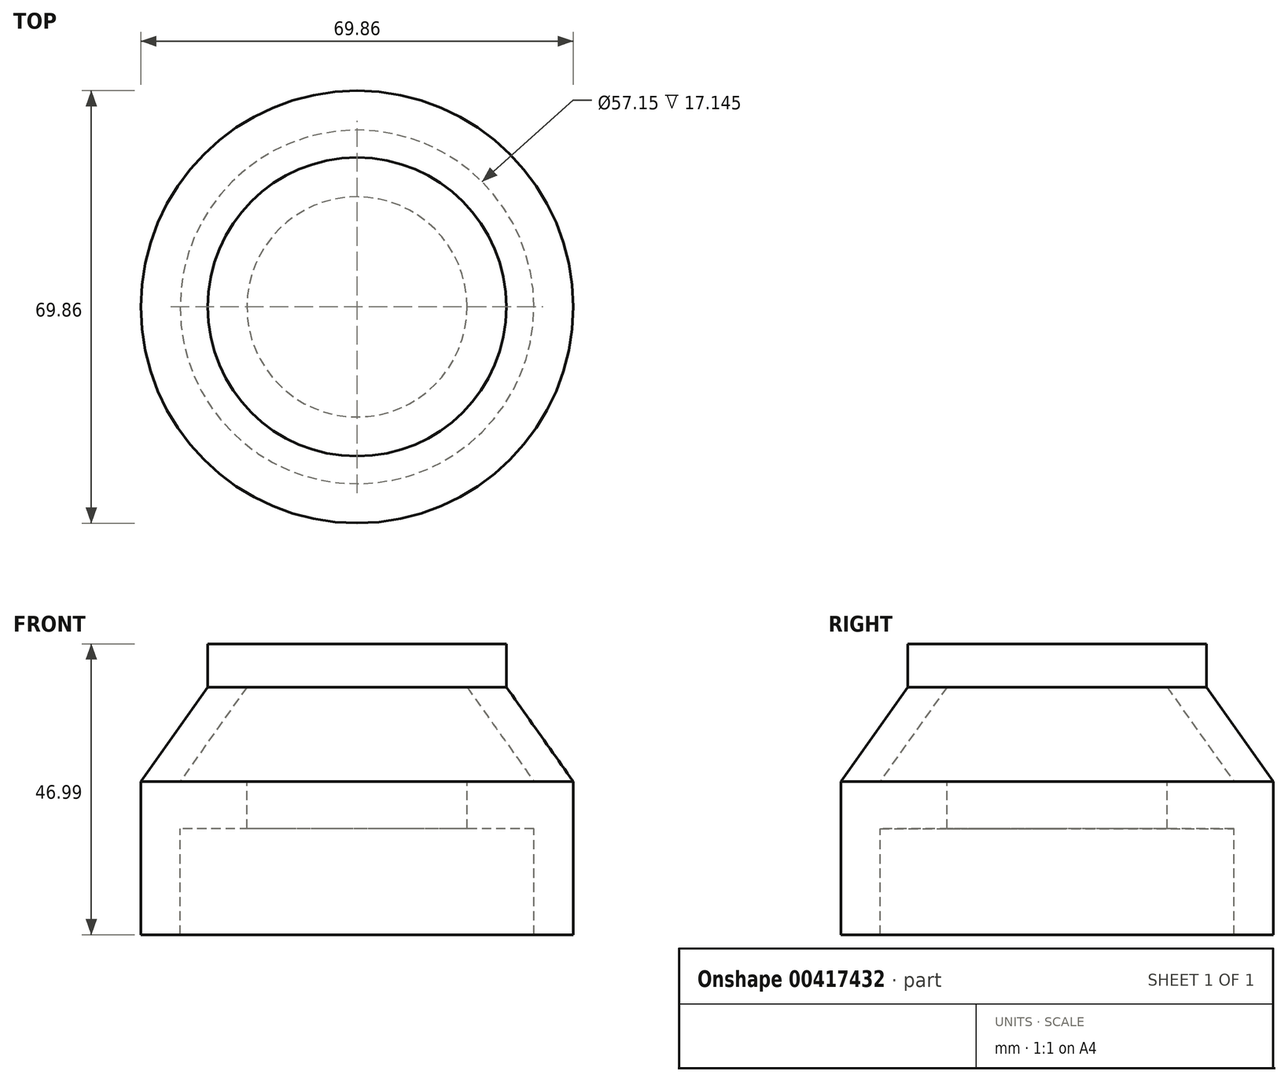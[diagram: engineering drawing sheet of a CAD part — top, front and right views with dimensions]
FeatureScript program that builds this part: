
annotation { "Feature Type Name" : "Feature", "Feature Type Description" : "" }
export const myFeature = defineFeature(function(context is Context, id is Id, definition is map)
    precondition{}
    {
        {
            var Q0;
            Q0=qCreatedBy(makeId("Front.planeOp"),FACE);
            var sketch = newSketch(context, id + "F0", { "sketchPlane" : qUnion([Q0])});
            skLineSegment(sketch, "E0", {"start": v(0, 55) * mm, "end": v(0, -52.11) * mm, "construction": true});
            skLineSegment(sketch, "E1.bottom", {"start": v(28.58, 17.15) * mm, "end": v(34.93, 17.15) * mm});
            skLineSegment(sketch, "E1.top", {"start": v(28.58, 0) * mm, "end": v(34.93, 0) * mm});
            skLineSegment(sketch, "E1.left", {"start": v(28.58, 17.15) * mm, "end": v(28.58, 0) * mm});
            skLineSegment(sketch, "E1.right", {"start": v(34.93, 17.15) * mm, "end": v(34.93, 0) * mm});
            skLineSegment(sketch, "E2.bottom", {"start": v(34.93, 17.15) * mm, "end": v(17.78, 17.15) * mm});
            skLineSegment(sketch, "E2.top", {"start": v(34.93, 24.77) * mm, "end": v(17.78, 24.77) * mm});
            skLineSegment(sketch, "E2.left", {"start": v(34.93, 17.15) * mm, "end": v(34.93, 24.77) * mm});
            skLineSegment(sketch, "E2.right", {"start": v(17.78, 17.15) * mm, "end": v(17.78, 24.77) * mm});
            skLineSegment(sketch, "E3", {"start": v(34.92, 24.76) * mm, "end": v(24.13, 40) * mm});
            skLineSegment(sketch, "E4", {"start": v(24.13, 40) * mm, "end": v(17.78, 40) * mm});
            skLineSegment(sketch, "E5", {"start": v(17.78, 40) * mm, "end": v(28.57, 24.77) * mm});
            skLineSegment(sketch, "E6.bottom", {"start": v(24.13, 40) * mm, "end": v(0, 40) * mm});
            skLineSegment(sketch, "E6.top", {"start": v(24.13, 47) * mm, "end": v(0, 47) * mm});
            skLineSegment(sketch, "E6.left", {"start": v(24.13, 40) * mm, "end": v(24.13, 47) * mm});
            skLineSegment(sketch, "E6.right", {"start": v(0, 40) * mm, "end": v(0, 47) * mm});
            skSolve(sketch);
        }
        {
            var Q0;
            {var subQ0=sQuery(id+"F0.wireOp",EDGE,"E3");Q0=makeQuery(id+"F0.imprint","IMPRINT",FACE,{"disambiguationData":[TD([[makeQuery(id+"F0.imprint","IMPRINT",EDGE,{"derivedFrom":subQ0}),1.0]])]});}
            var Q1;
            Q1=makeQuery(id+"F0.imprint","IMPRINT",FACE,{"disambiguationData":[TD([[makeQuery(id+"F0.imprint","IMPRINT",EDGE,{"derivedFrom":sQuery(id+"F0.wireOp",EDGE,"E6.top")}),1.0]])]});
            var Q2;
            {var subQ3=sQuery(id+"F0.wireOp",EDGE,"E2.left");Q2=makeQuery(id+"F0.imprint","IMPRINT",FACE,{"disambiguationData":[TD([[makeQuery(id+"F0.imprint","IMPRINT",EDGE,{"derivedFrom":subQ3}),1.0]])]});}
            var Q3;
            Q3=makeQuery(id+"F0.imprint","IMPRINT",FACE,{"disambiguationData":[TD([[makeQuery(id+"F0.imprint","IMPRINT",EDGE,{"derivedFrom":sQuery(id+"F0.wireOp",EDGE,"E1.top")}),1.0]])]});
            var Q4;
            Q4=sQuery(id+"F0.wireOp",EDGE,"E0");
            revolve(context, id + "F1", {"entities" : qUnion([Q0, Q1, Q2, Q3]), "axis" : qUnion([Q4]), "revolveType" : RevolveType.FULL});
        }
    });
